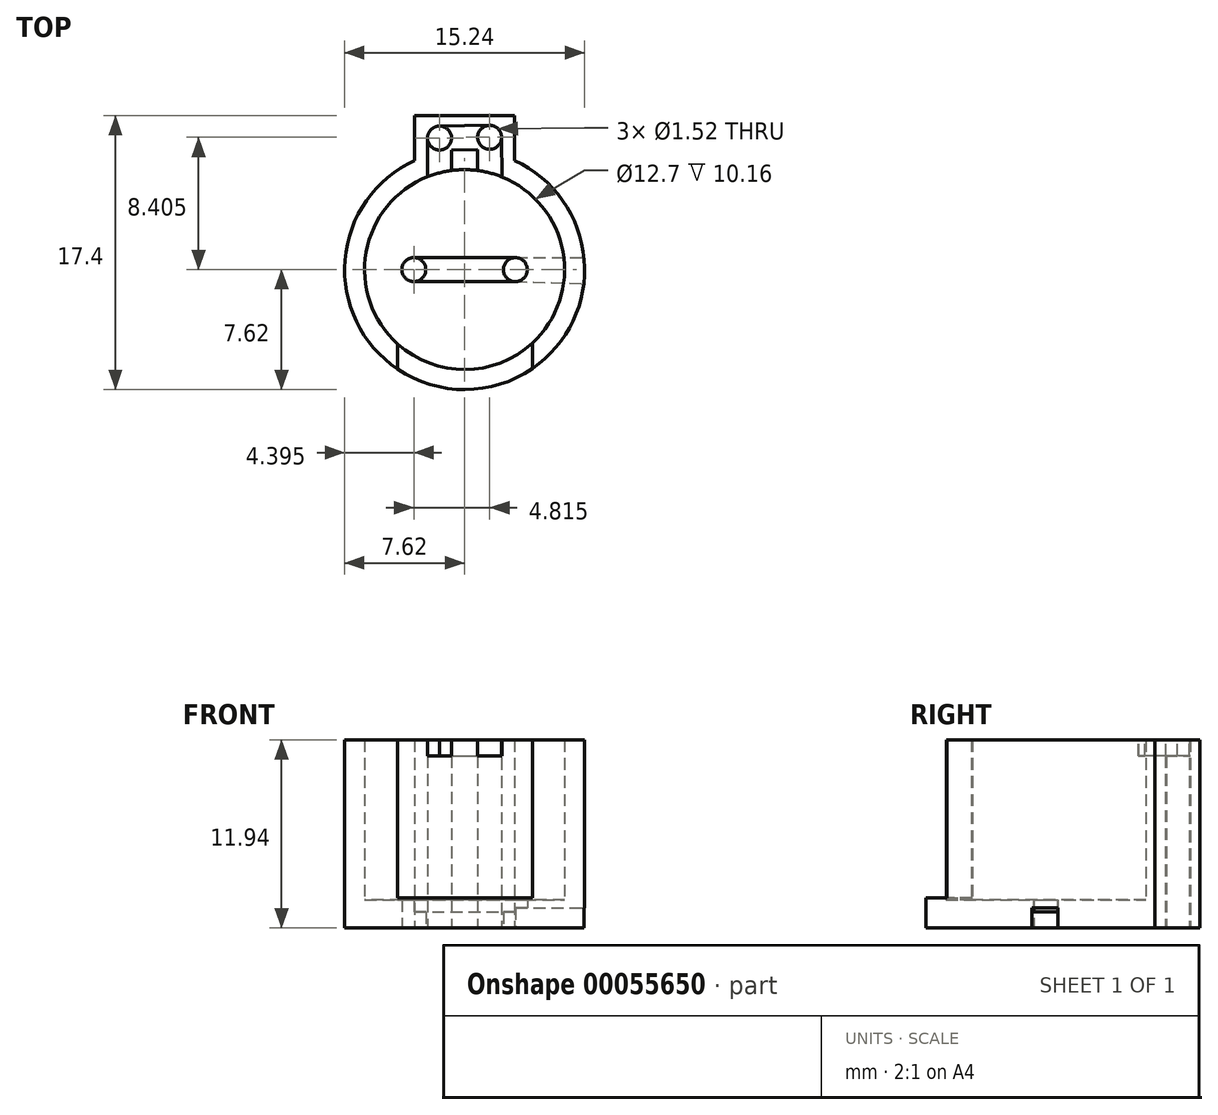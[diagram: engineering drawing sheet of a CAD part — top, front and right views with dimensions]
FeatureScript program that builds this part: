
annotation { "Feature Type Name" : "Feature", "Feature Type Description" : "" }
export const myFeature = defineFeature(function(context is Context, id is Id, definition is map)
    precondition{}
    {
        {
            var Q0;
            Q0=qCreatedBy(makeId("Top.planeOp"),FACE);
            var sketch = newSketch(context, id + "F0", { "sketchPlane" : qUnion([Q0])});
            skCircle(sketch, "E0", {"center": v(0, 0) * mm, "radius": 6.35 * mm});
            skArc(sketch, "E1", {"start": v(-3.18, 6.93) * mm, "mid": v(0, -7.62) * mm, "end": v(3.17, 6.93) * mm});
            skLineSegment(sketch, "E2.rect.top", {"start": v(3.18, 9.78) * mm, "end": v(-3.18, 9.78) * mm});
            skLineSegment(sketch, "E2.rect.left", {"start": v(3.17, 6.93) * mm, "end": v(3.17, 9.78) * mm});
            skLineSegment(sketch, "E2.rect.right", {"start": v(-3.18, 6.93) * mm, "end": v(-3.18, 9.78) * mm});
            skPoint(sketch, "E2.rect.middle", {"position": v(0, 8.36) * mm});
            skCircle(sketch, "E3", {"center": v(1.6, 8.4) * mm, "radius": 0.76 * mm});
            skCircle(sketch, "E4", {"center": v(-1.6, 8.36) * mm, "radius": 0.76 * mm});
            skLineSegment(sketch, "E5", {"start": v(0, 0) * mm, "end": v(0, 13.09) * mm, "construction": true});
            skLineSegment(sketch, "E6", {"start": v(-1.6, 8.36) * mm, "end": v(0, 8.36) * mm, "construction": true});
            skLineSegment(sketch, "E7", {"start": v(1.6, 8.4) * mm, "end": v(0, 8.36) * mm, "construction": true});
            skCircle(sketch, "E8", {"center": v(-3.22, 0) * mm, "radius": 0.76 * mm});
            skCircle(sketch, "E9", {"center": v(3.22, 0) * mm, "radius": 0.76 * mm});
            skLineSegment(sketch, "E10", {"start": v(-3.22, 0) * mm, "end": v(0, 0) * mm});
            skLineSegment(sketch, "E11", {"start": v(3.22, 0) * mm, "end": v(0, 0) * mm, "construction": true});
            skSolve(sketch);
        }
        {
            var Q0;
            Q0=makeQuery(id+"F0.imprint","IMPRINT",FACE,{"disambiguationData":[TD([[makeQuery(id+"F0.imprint","IMPRINT",EDGE,{"derivedFrom":sQuery(id+"F0.wireOp",EDGE,"E0")}),-1.0]])]});
            extrude(context, id + "F1", {"entities" : qUnion([Q0]), "depth" : 11.94 * mm});
        }
        {
            var Q0;
            Q0 = qSketchRegion(id + "F0", true);
            var Q1;
            Q1=makeQuery(id+"F0.imprint","IMPRINT",FACE,{"disambiguationData":[TD([[makeQuery(id+"F0.imprint","IMPRINT",EDGE,{"derivedFrom":sQuery(id+"F0.wireOp",EDGE,"E0")}),1.0]])]});
            extrude(context, id + "F2", {"entities" : qUnion([Q0, Q1]), "operationType" : NewBodyOperationType.ADD, "depth" : 1.78 * mm});
        }
        {
            var Q0;
            Q0=makeQuery(id+"F1.opExtrude","CAP_FACE",FACE,{"disambiguationData":[OSD([sQuery(id+"F0.wireOp",EDGE,"E0"),sQuery(id+"F0.wireOp",EDGE,"E1"),sQuery(id+"F0.wireOp",EDGE,"E2.rect.top"),sQuery(id+"F0.wireOp",EDGE,"E2.rect.left"),sQuery(id+"F0.wireOp",EDGE,"E2.rect.right"),sQuery(id+"F0.wireOp",EDGE,"E3"),sQuery(id+"F0.wireOp",EDGE,"E4")])],"isStart":false});
            var sketch = newSketch(context, id + "F3", { "sketchPlane" : qUnion([Q0])});
            skLineSegment(sketch, "E12", {"start": v(-1.62, 9.12) * mm, "end": v(1.58, 9.17) * mm});
            skLineSegment(sketch, "E13", {"start": v(-0.83, 7.6) * mm, "end": v(0.83, 7.63) * mm});
            skLineSegment(sketch, "E14", {"start": v(-2.35, 8.36) * mm, "end": v(-2.35, 5.9) * mm});
            skPoint(sketch, "E14.startSnap0", {"position": v(-3.18, 8.36) * mm});
            skLineSegment(sketch, "E15", {"start": v(-0.83, 7.6) * mm, "end": v(-0.83, 6.3) * mm});
            skLineSegment(sketch, "E16", {"start": v(0.83, 7.63) * mm, "end": v(0.83, 6.3) * mm});
            skLineSegment(sketch, "E17", {"start": v(2.35, 8.36) * mm, "end": v(2.39, 5.88) * mm});
            skPoint(sketch, "E18.orphan", {"position": v(-0.83, 8.36) * mm});
            skPoint(sketch, "E19.orphan", {"position": v(0.83, 8.36) * mm});
            skSolve(sketch);
        }
        {
            var Q0;
            {var subQ0=sQuery(id+"F3.wireOp",EDGE,"E12");var subQ1=makeQuery(id+"F1.opExtrude","CAP_EDGE",EDGE,{"disambiguationData":[OSD([sQuery(id+"F0.wireOp",EDGE,"E3")])],"isStart":false});var subQ2=makeQuery(id+"F3.imprint","INTERSECT",VERTEX,{"derivedFrom":[subQ1,subQ0]});Q0=makeQuery(id+"F3.imprint","IMPRINT",FACE,{"disambiguationData":[TD([[makeQuery(id+"F3.imprint","IMPRINT",EDGE,{"disambiguationData":[TD([[subQ2,1.0]])],"derivedFrom":subQ0}),-1.0]])]});}
            extrude(context, id + "F4", {"entities" : qUnion([Q0]), "operationType" : NewBodyOperationType.REMOVE, "oppositeDirection" : true, "depth" : 1.02 * mm});
        }
        {
            var Q0;
            Q0=makeQuery(id+"F2.opExtrude","CAP_FACE",FACE,{"disambiguationData":[OSD([sQuery(id+"F0.wireOp",EDGE,"E1"),sQuery(id+"F0.wireOp",EDGE,"E2.rect.top"),sQuery(id+"F0.wireOp",EDGE,"E2.rect.left"),sQuery(id+"F0.wireOp",EDGE,"E2.rect.right"),sQuery(id+"F0.wireOp",EDGE,"E3"),sQuery(id+"F0.wireOp",EDGE,"E4"),sQuery(id+"F0.wireOp",EDGE,"E8"),sQuery(id+"F0.wireOp",EDGE,"E9")])],"isStart":false});
            var sketch = newSketch(context, id + "F5", { "sketchPlane" : qUnion([Q0])});
            skLineSegment(sketch, "E20", {"start": v(-3.26, 0.76) * mm, "end": v(3.22, 0.76) * mm});
            skLineSegment(sketch, "E21", {"start": v(-3.26, -0.76) * mm, "end": v(3.22, -0.76) * mm});
            skSolve(sketch);
        }
        {
            var Q0;
            {var subQ0=sQuery(id+"F5.wireOp",EDGE,"E20");var subQ1=makeQuery(id+"F2.opExtrude","CAP_EDGE",EDGE,{"disambiguationData":[OSD([sQuery(id+"F0.wireOp",EDGE,"E9")])],"isStart":false});var subQ2=makeQuery(id+"F5.imprint","INTERSECT",VERTEX,{"derivedFrom":[subQ1,subQ0]});Q0=makeQuery(id+"F5.imprint","IMPRINT",FACE,{"disambiguationData":[TD([[makeQuery(id+"F5.imprint","IMPRINT",EDGE,{"disambiguationData":[TD([[subQ2,1.0]])],"derivedFrom":subQ0}),-1.0]])]});}
            extrude(context, id + "F6", {"entities" : qUnion([Q0]), "operationType" : NewBodyOperationType.REMOVE, "oppositeDirection" : true, "depth" : 0.76 * mm});
        }
        {
            var Q0;
            Q0=qCreatedBy(makeId("Front.planeOp"),FACE);
            cPlane(context, id + "F7", {"entities" : qUnion([Q0]), "cplaneType" : CPlaneType.OFFSET, "offset" : 6.6 * mm, "width" : 152.4 * mm, "height" : 152.4 * mm});
        }
        {
            var Q0;
            Q0=qCreatedBy(id+"F7.planeOp",FACE);
            var sketch = newSketch(context, id + "F8", { "sketchPlane" : qUnion([Q0])});
            skLineSegment(sketch, "E22.bottom", {"start": v(-4.25, 12.5) * mm, "end": v(4.3, 12.5) * mm});
            skLineSegment(sketch, "E22.top", {"start": v(-4.25, 1.9) * mm, "end": v(4.3, 1.9) * mm});
            skLineSegment(sketch, "E22.left", {"start": v(-4.25, 12.5) * mm, "end": v(-4.25, 1.9) * mm});
            skLineSegment(sketch, "E22.right", {"start": v(4.3, 12.5) * mm, "end": v(4.3, 1.9) * mm});
            skSolve(sketch);
        }
        {
            var Q0;
            Q0=makeQuery(id+"F8.imprint","IMPRINT",FACE,{"disambiguationData":[TD([[makeQuery(id+"F8.imprint","IMPRINT",EDGE,{"derivedFrom":sQuery(id+"F8.wireOp",EDGE,"E22.bottom")}),-1.0]])]});
            extrude(context, id + "F9", {"entities" : qUnion([Q0]), "operationType" : NewBodyOperationType.REMOVE, "oppositeDirection" : true, "depth" : 3.8 * mm, "hasSecondDirection" : true, "secondDirectionOppositeDirection" : false, "secondDirectionDepth" : 3.8 * mm});
        }
        {
            var Q0;
            {var subQ0=sQuery(id+"F0.wireOp",EDGE,"E4");var subQ1=sQuery(id+"F0.wireOp",EDGE,"E3");var subQ2=sQuery(id+"F0.wireOp",EDGE,"E2.rect.right");var subQ3=sQuery(id+"F0.wireOp",EDGE,"E2.rect.left");var subQ4=sQuery(id+"F0.wireOp",EDGE,"E2.rect.top");var subQ5=sQuery(id+"F0.wireOp",EDGE,"E1");Q0=makeQuery(id+"F2.boolean.opBoolean","MERGE",FACE,{"derivedFrom":[makeQuery(id+"F1.opExtrude","CAP_FACE",FACE,{"disambiguationData":[OSD([sQuery(id+"F0.wireOp",EDGE,"E0"),subQ5,subQ4,subQ3,subQ2,subQ1,subQ0])],"isStart":true}),makeQuery(id+"F2.opExtrude","CAP_FACE",FACE,{"disambiguationData":[OSD([subQ5,subQ4,subQ3,subQ2,subQ1,subQ0,sQuery(id+"F0.wireOp",EDGE,"E8"),sQuery(id+"F0.wireOp",EDGE,"E9")])],"isStart":true})]});}
            var sketch = newSketch(context, id + "F10", { "sketchPlane" : qUnion([Q0])});
            skLineSegment(sketch, "E23", {"start": v(3.2, 0.76) * mm, "end": v(7.57, 0.88) * mm});
            skLineSegment(sketch, "E24", {"start": v(3.2, -0.76) * mm, "end": v(7.58, -0.76) * mm});
            skSolve(sketch);
        }
        {
            var Q0;
            {var subQ0=sQuery(id+"F10.wireOp",EDGE,"E23");Q0=makeQuery(id+"F10.imprint","IMPRINT",FACE,{"disambiguationData":[TD([[makeQuery(id+"F10.imprint","IMPRINT",EDGE,{"derivedFrom":subQ0}),-1.0]])]});}
            extrude(context, id + "F11", {"entities" : qUnion([Q0]), "operationType" : NewBodyOperationType.REMOVE, "oppositeDirection" : true, "depth" : 1.27 * mm});
        }
    });
